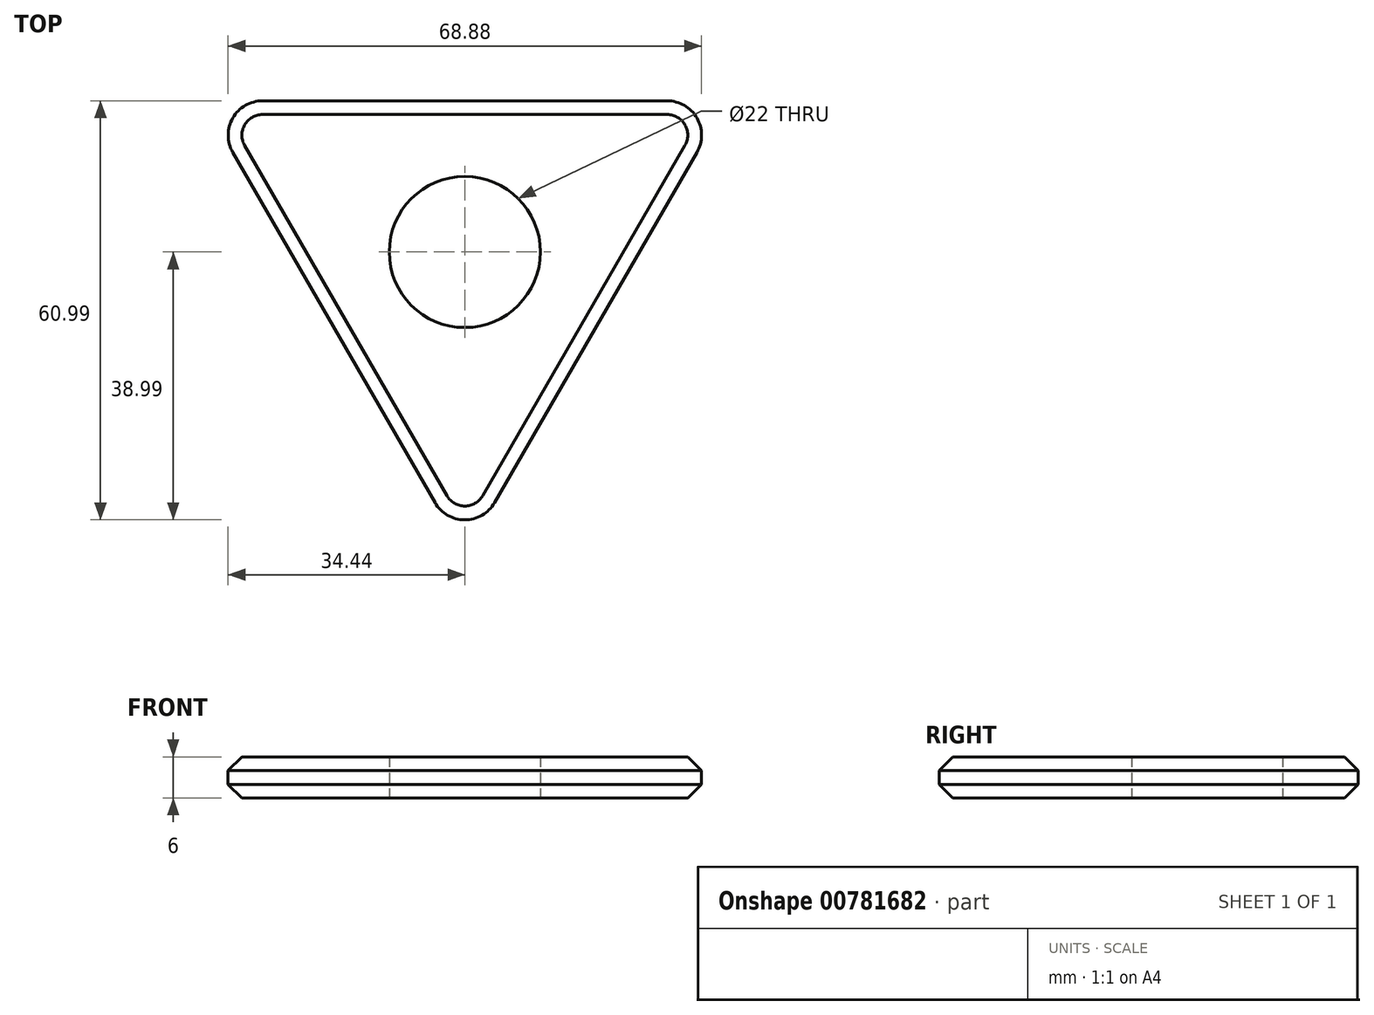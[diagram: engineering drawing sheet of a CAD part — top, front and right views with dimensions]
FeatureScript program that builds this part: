
annotation { "Feature Type Name" : "Feature", "Feature Type Description" : "" }
export const myFeature = defineFeature(function(context is Context, id is Id, definition is map)
    precondition{}
    {
        {
            var Q0;
            Q0=qCreatedBy(makeId("Top.planeOp"),FACE);
            var sketch = newSketch(context, id + "F0", { "sketchPlane" : qUnion([Q0])});
            skCircle(sketch, "E0.cCircle", {"center": v(0, 0) * mm, "radius": 22 * mm, "construction": true});
            skLineSegment(sketch, "E0.0", {"start": v(-29.44, 22) * mm, "end": v(29.44, 22) * mm});
            skLineSegment(sketch, "E0.1", {"start": v(33.77, 14.5) * mm, "end": v(4.33, -36.5) * mm});
            skLineSegment(sketch, "E0.2", {"start": v(-4.33, -36.5) * mm, "end": v(-33.77, 14.5) * mm});
            skPoint(sketch, "E0.0.midPoint", {"position": v(0, 22) * mm});
            skPoint(sketch, "E1.visualSharp", {"position": v(-38.1, 22) * mm});
            skArc(sketch, "E1.filletArc", {"start": v(-29.44, 22) * mm, "mid": v(-33.77, 19.5) * mm, "end": v(-33.77, 14.5) * mm});
            skPoint(sketch, "E2.visualSharp", {"position": v(38.1, 22) * mm});
            skArc(sketch, "E2.filletArc", {"start": v(33.77, 14.5) * mm, "mid": v(33.77, 19.5) * mm, "end": v(29.44, 22) * mm});
            skPoint(sketch, "E3.visualSharp", {"position": v(0, -44) * mm});
            skArc(sketch, "E3.filletArc", {"start": v(-4.33, -36.5) * mm, "mid": v(0, -39) * mm, "end": v(4.33, -36.5) * mm});
            skCircle(sketch, "E4", {"center": v(0, 0) * mm, "radius": 11 * mm});
            skSolve(sketch);
        }
        {
            var Q0;
            Q0=makeQuery(id+"F0.imprint","IMPRINT",FACE,{"disambiguationData":[TD([[makeQuery(id+"F0.imprint","IMPRINT",EDGE,{"derivedFrom":sQuery(id+"F0.wireOp",EDGE,"E0.0")}),-1.0]])]});
            extrude(context, id + "F1", {"entities" : qUnion([Q0]), "depth" : 6 * mm, "offsetDistance" : 25 * mm});
        }
        {
            var Q0;
            Q0=makeQuery(id+"F1.opExtrude","CAP_EDGE",EDGE,{"disambiguationData":[OSD([sQuery(id+"F0.wireOp",EDGE,"E0.2")])],"isStart":false});
            var Q1;
            Q1=makeQuery(id+"F1.opExtrude","CAP_EDGE",EDGE,{"disambiguationData":[OSD([sQuery(id+"F0.wireOp",EDGE,"E0.2")])],"isStart":true});
            var Q2;
            Q2=makeQuery(id+"F1.opExtrude","CAP_EDGE",EDGE,{"disambiguationData":[OSD([sQuery(id+"F0.wireOp",EDGE,"E0.0")])],"isStart":false});
            chamfer(context, id + "F2", {"entities" : qUnion([Q0, Q1, Q2]), "width" : 2 * mm, "tangentPropagation" : true});
        }
        {
            var Q0;
            Q0=qCreatedBy(makeId("Top.planeOp"),FACE);
            var sketch = newSketch(context, id + "F3", { "sketchPlane" : qUnion([Q0])});
            skCircle(sketch, "E5.cCircle", {"center": v(-23.7, 14.1) * mm, "radius": 4.2 * mm, "construction": true});
            skLineSegment(sketch, "E5.0", {"start": v(-19.54, 11.6) * mm, "end": v(-23.8, 9.25) * mm});
            skLineSegment(sketch, "E5.1", {"start": v(-23.8, 9.25) * mm, "end": v(-27.96, 11.77) * mm});
            skLineSegment(sketch, "E5.2", {"start": v(-27.96, 11.77) * mm, "end": v(-27.86, 16.63) * mm});
            skLineSegment(sketch, "E5.3", {"start": v(-27.86, 16.63) * mm, "end": v(-23.6, 18.97) * mm});
            skLineSegment(sketch, "E5.4", {"start": v(-23.6, 18.97) * mm, "end": v(-19.44, 16.45) * mm});
            skLineSegment(sketch, "E5.5", {"start": v(-19.44, 16.45) * mm, "end": v(-19.54, 11.6) * mm});
            skPoint(sketch, "E5.0.midPoint", {"position": v(-21.67, 10.42) * mm});
            skSolve(sketch);
        }
        {
            var Q0;
            Q0=makeQuery(id+"F3.imprint","IMPRINT",FACE,{"disambiguationData":[TD([[makeQuery(id+"F3.imprint","IMPRINT",EDGE,{"derivedFrom":sQuery(id+"F3.wireOp",EDGE,"E5.0")}),-1.0]])]});
            extrude(context, id + "F4", {"entities" : qUnion([Q0]), "operationType" : NewBodyOperationType.REMOVE, "depth" : 25 * mm, "offsetDistance" : 25 * mm});
        }
        {
            var Q0;
            Q0=makeQuery(id+"F1.opExtrude","CAP_FACE",FACE,{"disambiguationData":[OSD([sQuery(id+"F0.wireOp",EDGE,"E0.0"),sQuery(id+"F0.wireOp",EDGE,"E0.1"),sQuery(id+"F0.wireOp",EDGE,"E0.2"),sQuery(id+"F0.wireOp",EDGE,"E1.filletArc"),sQuery(id+"F0.wireOp",EDGE,"E2.filletArc"),sQuery(id+"F0.wireOp",EDGE,"E3.filletArc"),sQuery(id+"F0.wireOp",EDGE,"E4")])],"isStart":false});
            var sketch = newSketch(context, id + "F5", { "sketchPlane" : qUnion([Q0])});
            skSolve(sketch);
        }
        {
            var Q0;
            {var subQ0=makeQuery(id+"F1.opExtrude","CAP_FACE",FACE,{"disambiguationData":[OSD([sQuery(id+"F0.wireOp",EDGE,"E0.0"),sQuery(id+"F0.wireOp",EDGE,"E0.1"),sQuery(id+"F0.wireOp",EDGE,"E0.2"),sQuery(id+"F0.wireOp",EDGE,"E1.filletArc"),sQuery(id+"F0.wireOp",EDGE,"E2.filletArc"),sQuery(id+"F0.wireOp",EDGE,"E3.filletArc"),sQuery(id+"F0.wireOp",EDGE,"E4")])],"isStart":false});Q0=makeQuery(id+"F5.imprint","IMPRINT",FACE,{"disambiguationData":[TD([[makeQuery(id+"F5.imprint","IMPRINT",EDGE,{"derivedFrom":makeQuery(id+"F4.boolean.opBoolean","INTERSECT",EDGE,{"derivedFrom":[subQ0,makeQuery(id+"F4.opExtrude","SWEPT_FACE",FACE,{"disambiguationData":[OSD([sQuery(id+"F3.wireOp",EDGE,"E5.0")])]})]})}),1.0]])]});}
            var sketch = newSketch(context, id + "F6", { "sketchPlane" : qUnion([Q0])});
            skSolve(sketch);
        }
        {
            var Q0;
            {var subQ0=makeQuery(id+"F1.opExtrude","CAP_FACE",FACE,{"disambiguationData":[OSD([sQuery(id+"F0.wireOp",EDGE,"E0.0"),sQuery(id+"F0.wireOp",EDGE,"E0.1"),sQuery(id+"F0.wireOp",EDGE,"E0.2"),sQuery(id+"F0.wireOp",EDGE,"E1.filletArc"),sQuery(id+"F0.wireOp",EDGE,"E2.filletArc"),sQuery(id+"F0.wireOp",EDGE,"E3.filletArc"),sQuery(id+"F0.wireOp",EDGE,"E4")])],"isStart":false});Q0=makeQuery(id+"F6.imprint","IMPRINT",FACE,{"disambiguationData":[TD([[makeQuery(id+"F6.imprint","IMPRINT",EDGE,{"derivedFrom":makeQuery(id+"F5.imprint","IMPRINT",EDGE,{"derivedFrom":makeQuery(id+"F4.boolean.opBoolean","INTERSECT",EDGE,{"derivedFrom":[subQ0,makeQuery(id+"F4.opExtrude","SWEPT_FACE",FACE,{"disambiguationData":[OSD([sQuery(id+"F3.wireOp",EDGE,"E5.0")])]})]})})}),1.0]])]});}
            extrude(context, id + "F7", {"entities" : qUnion([Q0]), "operationType" : NewBodyOperationType.ADD, "oppositeDirection" : true, "depth" : 6 * mm, "offsetDistance" : 25 * mm});
        }
    });
